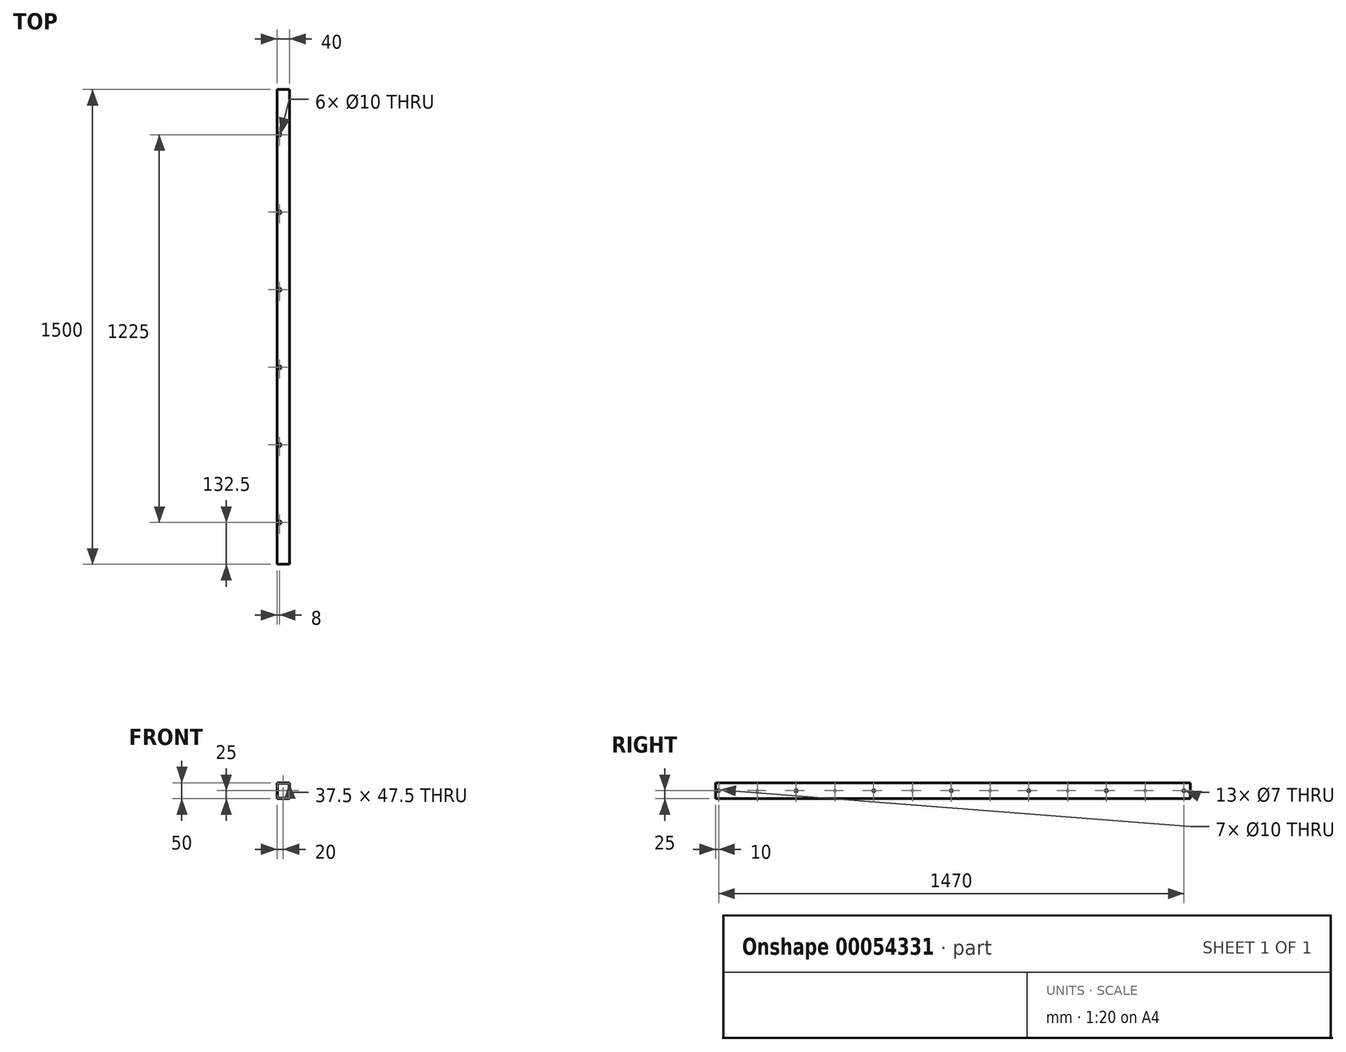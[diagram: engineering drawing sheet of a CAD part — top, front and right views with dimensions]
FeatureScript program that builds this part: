
annotation { "Feature Type Name" : "Feature", "Feature Type Description" : "" }
export const myFeature = defineFeature(function(context is Context, id is Id, definition is map)
    precondition{}
    {
        {
            var Q0;
            Q0=qCreatedBy(makeId("Front.planeOp"),FACE);
            var sketch = newSketch(context, id + "F0", { "sketchPlane" : qUnion([Q0])});
            skLineSegment(sketch, "E0.rect.bottom", {"start": v(-20, 25) * mm, "end": v(20, 25) * mm});
            skLineSegment(sketch, "E0.rect.top", {"start": v(-20, -25) * mm, "end": v(20, -25) * mm});
            skLineSegment(sketch, "E0.rect.left", {"start": v(-20, 25) * mm, "end": v(-20, -25) * mm});
            skLineSegment(sketch, "E0.rect.right", {"start": v(20, 25) * mm, "end": v(20, -25) * mm});
            skPoint(sketch, "E0.rect.middle", {"position": v(0, 0) * mm});
            skLineSegment(sketch, "E1.0", {"start": v(-18.75, 23.75) * mm, "end": v(18.75, 23.75) * mm});
            skLineSegment(sketch, "E1.1", {"start": v(-18.75, 23.75) * mm, "end": v(-18.75, -23.75) * mm});
            skLineSegment(sketch, "E1.2", {"start": v(-18.75, -23.75) * mm, "end": v(18.75, -23.75) * mm});
            skLineSegment(sketch, "E1.3", {"start": v(18.75, 23.75) * mm, "end": v(18.75, -23.75) * mm});
            skSolve(sketch);
        }
        {
            var Q0;
            Q0=makeQuery(id+"F0.imprint","IMPRINT",FACE,{"disambiguationData":[TD([[makeQuery(id+"F0.imprint","IMPRINT",EDGE,{"derivedFrom":sQuery(id+"F0.wireOp",EDGE,"E0.rect.bottom")}),-1.0]])]});
            extrude(context, id + "F1", {"entities" : qUnion([Q0]), "depth" : 1500 * mm});
        }
        {
            var Q0;
            Q0=makeQuery(id+"F1.opExtrude","SWEPT_FACE",FACE,{"disambiguationData":[OSD([sQuery(id+"F0.wireOp",EDGE,"E0.rect.left")])]});
            var sketch = newSketch(context, id + "F2", { "sketchPlane" : qUnion([Q0])});
            skPoint(sketch, "E2", {"position": v(1490, 0) * mm});
            skPoint(sketch, "E3.1.0.0", {"position": v(1245, 0) * mm});
            skPoint(sketch, "E3.2.0.0", {"position": v(1000, 0) * mm});
            skPoint(sketch, "E3.3.0.0", {"position": v(755, 0) * mm});
            skPoint(sketch, "E3.4.0.0", {"position": v(510, 0) * mm});
            skLineSegment(sketch, "E3.direction1", {"start": v(1490, 0) * mm, "end": v(1245, 0) * mm, "construction": true});
            skPoint(sketch, "E4", {"position": v(1367.5, 0) * mm});
            skPoint(sketch, "E5.1.0.0", {"position": v(1122.5, 0) * mm});
            skPoint(sketch, "E5.2.0.0", {"position": v(877.5, 0) * mm});
            skPoint(sketch, "E5.3.0.0", {"position": v(632.5, 0) * mm});
            skLineSegment(sketch, "E5.direction1", {"start": v(1367.5, 0) * mm, "end": v(1122.5, 0) * mm, "construction": true});
            skPoint(sketch, "E6.0.4.0", {"position": v(387.5, 0) * mm});
            skPoint(sketch, "E6.0.5.0", {"position": v(142.5, 0) * mm});
            skPoint(sketch, "E7.0.5.0", {"position": v(265, 0) * mm});
            skPoint(sketch, "E7.0.6.0", {"position": v(20, 0) * mm});
            skSolve(sketch);
        }
        {
            var Q0;
            Q0=makeQuery(id+"F1.opExtrude","SWEPT_FACE",FACE,{"disambiguationData":[OSD([sQuery(id+"F0.wireOp",EDGE,"E0.rect.bottom")])]});
            var sketch = newSketch(context, id + "F3", { "sketchPlane" : qUnion([Q0])});
            skPoint(sketch, "E8", {"position": v(-12, -1367.5) * mm});
            skPoint(sketch, "E9.0.1.0", {"position": v(-12, -1122.5) * mm});
            skPoint(sketch, "E9.0.2.0", {"position": v(-12, -877.5) * mm});
            skPoint(sketch, "E9.0.3.0", {"position": v(-12, -632.5) * mm});
            skLineSegment(sketch, "E9.direction1", {"start": v(-12, -1367.5) * mm, "end": v(13, -1367.5) * mm, "construction": true});
            skLineSegment(sketch, "E9.direction2", {"start": v(-12, -1367.5) * mm, "end": v(-12, -1122.5) * mm, "construction": true});
            skPoint(sketch, "E10.0.0.4", {"position": v(-12, -387.5) * mm});
            skPoint(sketch, "E10.0.0.5", {"position": v(-12, -142.5) * mm});
            skSolve(sketch);
        }
        {
            var Q0;
            Q0=sQuery(id+"F2.wireOp",VERTEX,"E2");
            var Q1;
            Q1=sQuery(id+"F2.wireOp",VERTEX,"E3.1.0.0");
            var Q2;
            Q2=sQuery(id+"F2.wireOp",VERTEX,"E3.2.0.0");
            var Q3;
            Q3=sQuery(id+"F2.wireOp",VERTEX,"E3.3.0.0");
            var Q4;
            Q4=sQuery(id+"F2.wireOp",VERTEX,"E3.4.0.0");
            var Q5;
            Q5=sQuery(id+"F2.wireOp",VERTEX,"E7.0.5.0");
            var Q6;
            Q6=sQuery(id+"F2.wireOp",VERTEX,"E7.0.6.0");
            var Q7;
            Q7=makeQuery(id+"F1.opExtrude","SWEPT_BODY",BODY,{"disambiguationData":[OSD([sQuery(id+"F0.wireOp",EDGE,"E0.rect.bottom"),sQuery(id+"F0.wireOp",EDGE,"E0.rect.top"),sQuery(id+"F0.wireOp",EDGE,"E0.rect.left"),sQuery(id+"F0.wireOp",EDGE,"E0.rect.right"),sQuery(id+"F0.wireOp",EDGE,"E1.0"),sQuery(id+"F0.wireOp",EDGE,"E1.1"),sQuery(id+"F0.wireOp",EDGE,"E1.2"),sQuery(id+"F0.wireOp",EDGE,"E1.3")])]});
            hole(context, id + "F4", {"style" : HoleStyle.SIMPLE, "holeDiameter" : 7 * mm, "endStyle" : HoleEndStyle.THROUGH, "locations" : qUnion([Q0, Q1, Q2, Q3, Q4, Q5, Q6]), "scope" : qUnion([Q7])});
        }
        {
            var Q0;
            Q0=sQuery(id+"F2.wireOp",VERTEX,"E2");
            var Q1;
            Q1=sQuery(id+"F2.wireOp",VERTEX,"E3.1.0.0");
            var Q2;
            Q2=sQuery(id+"F2.wireOp",VERTEX,"E3.2.0.0");
            var Q3;
            Q3=sQuery(id+"F2.wireOp",VERTEX,"E3.3.0.0");
            var Q4;
            Q4=sQuery(id+"F2.wireOp",VERTEX,"E3.4.0.0");
            var Q5;
            Q5=sQuery(id+"F3.wireOp",VERTEX,"E8");
            var Q6;
            Q6=sQuery(id+"F3.wireOp",VERTEX,"E9.0.1.0");
            var Q7;
            Q7=sQuery(id+"F3.wireOp",VERTEX,"E9.0.2.0");
            var Q8;
            Q8=sQuery(id+"F3.wireOp",VERTEX,"E9.0.3.0");
            var Q9;
            Q9=sQuery(id+"F3.wireOp",VERTEX,"E10.0.0.4");
            var Q10;
            Q10=sQuery(id+"F3.wireOp",VERTEX,"E10.0.0.5");
            var Q11;
            Q11=sQuery(id+"F2.wireOp",VERTEX,"E7.0.5.0");
            var Q12;
            Q12=sQuery(id+"F2.wireOp",VERTEX,"E7.0.6.0");
            var Q13;
            Q13=makeQuery(id+"F1.opExtrude","SWEPT_BODY",BODY,{"disambiguationData":[OSD([sQuery(id+"F0.wireOp",EDGE,"E0.rect.bottom"),sQuery(id+"F0.wireOp",EDGE,"E0.rect.top"),sQuery(id+"F0.wireOp",EDGE,"E0.rect.left"),sQuery(id+"F0.wireOp",EDGE,"E0.rect.right"),sQuery(id+"F0.wireOp",EDGE,"E1.0"),sQuery(id+"F0.wireOp",EDGE,"E1.1"),sQuery(id+"F0.wireOp",EDGE,"E1.2"),sQuery(id+"F0.wireOp",EDGE,"E1.3")])]});
            hole(context, id + "F5", {"style" : HoleStyle.SIMPLE, "holeDiameter" : 10 * mm, "endStyle" : HoleEndStyle.BLIND, "holeDepth" : 20 * mm, "locations" : qUnion([Q0, Q1, Q2, Q3, Q4, Q5, Q6, Q7, Q8, Q9, Q10, Q11, Q12]), "scope" : qUnion([Q13])});
        }
        {
            var Q0;
            Q0=sQuery(id+"F2.wireOp",VERTEX,"E4");
            var Q1;
            Q1=sQuery(id+"F2.wireOp",VERTEX,"E5.1.0.0");
            var Q2;
            Q2=sQuery(id+"F2.wireOp",VERTEX,"E5.2.0.0");
            var Q3;
            Q3=sQuery(id+"F2.wireOp",VERTEX,"E5.3.0.0");
            var Q4;
            Q4=sQuery(id+"F2.wireOp",VERTEX,"E6.0.4.0");
            var Q5;
            Q5=sQuery(id+"F2.wireOp",VERTEX,"E6.0.5.0");
            var Q6;
            Q6=makeQuery(id+"F1.opExtrude","SWEPT_BODY",BODY,{"disambiguationData":[OSD([sQuery(id+"F0.wireOp",EDGE,"E0.rect.bottom"),sQuery(id+"F0.wireOp",EDGE,"E0.rect.top"),sQuery(id+"F0.wireOp",EDGE,"E0.rect.left"),sQuery(id+"F0.wireOp",EDGE,"E0.rect.right"),sQuery(id+"F0.wireOp",EDGE,"E1.0"),sQuery(id+"F0.wireOp",EDGE,"E1.1"),sQuery(id+"F0.wireOp",EDGE,"E1.2"),sQuery(id+"F0.wireOp",EDGE,"E1.3")])]});
            hole(context, id + "F6", {"style" : HoleStyle.SIMPLE, "holeDiameter" : 7 * mm, "endStyle" : HoleEndStyle.BLIND, "holeDepth" : 2 * mm, "locations" : qUnion([Q0, Q1, Q2, Q3, Q4, Q5]), "scope" : qUnion([Q6])});
        }
    });
